# Revit family: Legrand-Ups-Keor_MOD-125_250kVA
name_source: partatom
category: Installations électriques
revit_build: Autodesk Revit 2018 (Build: 20170223_1515(x64)
units: mm (PartAtom-declared; Revit-internal decimal feet)

## family parameters
Basée sur le plan de construction = Non
Conserver l'orientation des annotations = Non
Cote de connecteur circulaire = Utiliser le diamètre
Couper avec des vides une fois chargée = Non
Numéro OmniClass = 23.80.10.17.34
Partagée = Non
Point de calcul de pièce = Non
Titre OmniClass = Static Uninterruptible Power Supplies
Toujours verticalement = Oui
Type d'élément = Normal

## types (2) — shared parameters
Back Clearance = 200 mm  [stored 0.656168 ft]
Cabinet Depth = 970 mm  [stored 3.18241 ft]
Cabinet Height = 1990 mm  [stored 6.52887 ft]
Cabinet Width = 600 mm
Conductors = Cables
Connection constraint = Ahead and bottom
Connection constraint (signal) = Behind and above
Fabricant = LEGRAND
Frequency of use = 50 Hz or 60 Hz selectable
Front Clearance = 1500 mm  [stored 4.92126 ft]
General Conditions of Use = https://export.legrand.com
Humidity = 0-95% not condensing
Input / Output phase configuration = 3ph+N+PE/3ph+N+PE
Installation space = 1.15 m³
Installation type = On the floor
Max sound pressure level = 65
Modèle = TRIMOD HE
Number of installed PM (N° x kW) = 0
Number of installed battry (N°block - Ah) = 0
Operating altitude = up to 1000 m altitude without derating
Operating temperature = from 0°C to +40°C
Output Voltage = 380,400,415 Vac
Output power factor = 1
URL = https://ups.legrand.com
Visibilità aree d'installazione = Oui
zero-valued in all types: Side Clearance

## per-type parameters (varying)
| type | Active power of use | Max number of PM (N° x kW) | Max number of battery drawer (N°block - Ah) | Nominal Power | Weight |
| LG-310480 | 125 kW | 5 x 25 kW | 10 | 125 kVA | 205.0 kg |
| LG-310481 | 250 kW | 10 x 25 kW | 0 | 250 kVA | 190.0 kg |

note: [stored X ft] marks values corroborated as IEEE doubles in the binary element streams (Revit-internal decimal feet)
